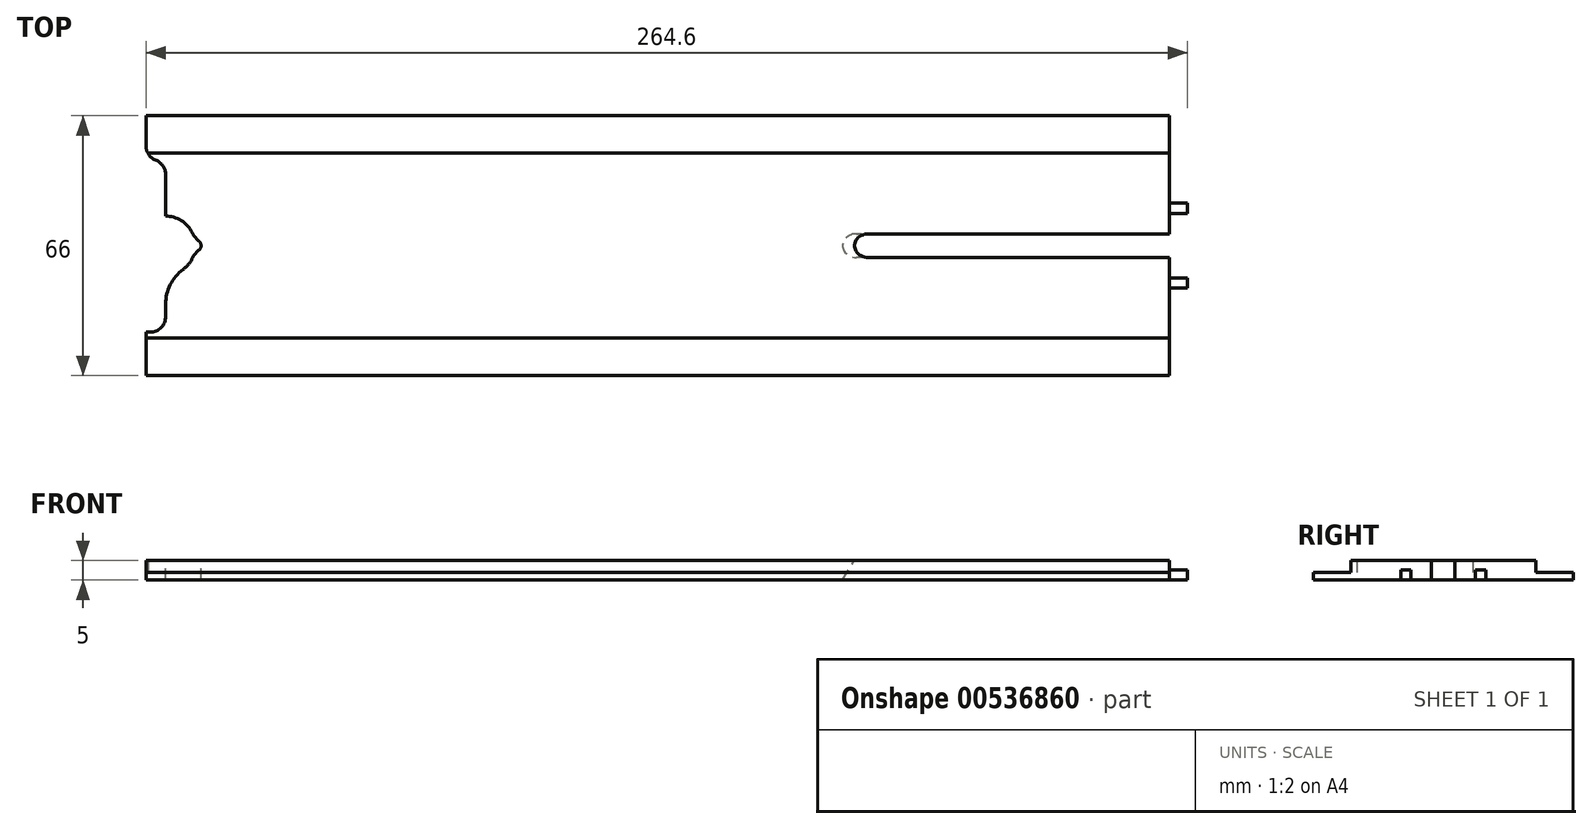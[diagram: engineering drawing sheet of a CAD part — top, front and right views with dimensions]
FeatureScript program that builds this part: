
annotation { "Feature Type Name" : "Feature", "Feature Type Description" : "" }
export const myFeature = defineFeature(function(context is Context, id is Id, definition is map)
    precondition{}
    {
        {
            var Q0;
            Q0=qCreatedBy(makeId("Top.planeOp"),FACE);
            var sketch = newSketch(context, id + "F0", { "sketchPlane" : qUnion([Q0])});
            skLineSegment(sketch, "E0.bottom", {"start": v(-61.94, 24.83) * mm, "end": v(198.06, 24.83) * mm});
            skLineSegment(sketch, "E0.top", {"start": v(-61.94, -41.17) * mm, "end": v(198.06, -41.17) * mm});
            skLineSegment(sketch, "E0.left", {"start": v(-61.94, 24.83) * mm, "end": v(-61.94, -41.17) * mm});
            skLineSegment(sketch, "E0.right", {"start": v(198.06, 24.83) * mm, "end": v(198.06, -41.17) * mm});
            skSolve(sketch);
        }
        {
            var Q0;
            Q0=makeQuery(id+"F0.imprint","IMPRINT",FACE,{"disambiguationData":[TD([[makeQuery(id+"F0.imprint","IMPRINT",EDGE,{"derivedFrom":sQuery(id+"F0.wireOp",EDGE,"E0.bottom")}),-1.0]])]});
            extrude(context, id + "F1", {"entities" : qUnion([Q0]), "depth" : 2 * mm, "offsetDistance" : 25 * mm});
        }
        {
            var Q0;
            Q0=makeQuery(id+"F1.opExtrude","CAP_FACE",FACE,{"disambiguationData":[OSD([sQuery(id+"F0.wireOp",EDGE,"E0.bottom"),sQuery(id+"F0.wireOp",EDGE,"E0.top"),sQuery(id+"F0.wireOp",EDGE,"E0.left"),sQuery(id+"F0.wireOp",EDGE,"E0.right")])],"isStart":false});
            var sketch = newSketch(context, id + "F2", { "sketchPlane" : qUnion([Q0])});
            skLineSegment(sketch, "E1.bottom", {"start": v(-61.94, 15.33) * mm, "end": v(198.06, 15.33) * mm});
            skLineSegment(sketch, "E1.top", {"start": v(-61.94, -31.67) * mm, "end": v(198.06, -31.67) * mm});
            skLineSegment(sketch, "E1.left", {"start": v(-61.94, 15.33) * mm, "end": v(-61.94, -31.67) * mm});
            skLineSegment(sketch, "E1.right", {"start": v(198.06, 15.33) * mm, "end": v(198.06, -31.67) * mm});
            skSolve(sketch);
        }
        {
            var Q0;
            Q0=qSketchRegion(id+"F2",true);
            extrude(context, id + "F3", {"entities" : qUnion([Q0]), "operationType" : NewBodyOperationType.ADD, "depth" : 3 * mm, "offsetDistance" : 25 * mm});
        }
        {
            var Q0;
            Q0=makeQuery(id+"F3.opExtrude","CAP_FACE",FACE,{"disambiguationData":[OSD([sQuery(id+"F2.wireOp",EDGE,"E1.bottom"),sQuery(id+"F2.wireOp",EDGE,"E1.top"),sQuery(id+"F2.wireOp",EDGE,"E1.left"),sQuery(id+"F2.wireOp",EDGE,"E1.right")])],"isStart":false});
            var sketch = newSketch(context, id + "F4", { "sketchPlane" : qUnion([Q0])});
            skLineSegment(sketch, "E2", {"start": v(198.06, -8.17) * mm, "end": v(-61.94, -8.17) * mm, "construction": true});
            skLineSegment(sketch, "E3.bottom", {"start": v(198.06, -5.17) * mm, "end": v(118.06, -5.17) * mm});
            skLineSegment(sketch, "E3.top", {"start": v(198.06, -11.17) * mm, "end": v(118.06, -11.17) * mm});
            skLineSegment(sketch, "E3.left", {"start": v(198.06, -5.17) * mm, "end": v(198.06, -11.17) * mm});
            skLineSegment(sketch, "E3.right", {"start": v(118.06, -5.17) * mm, "end": v(118.06, -11.17) * mm});
            skPoint(sketch, "E4", {"position": v(118.06, -8.17) * mm});
            skSolve(sketch);
        }
        {
            var Q0;
            Q0=qSketchRegion(id+"F4",true);
            extrude(context, id + "F5", {"entities" : qUnion([Q0]), "operationType" : NewBodyOperationType.REMOVE, "oppositeDirection" : true, "depth" : 25 * mm, "offsetDistance" : 25 * mm});
        }
        {
            var Q0;
            Q0=makeQuery(id+"F5.boolean.opBoolean","INTERSECT",EDGE,{"derivedFrom":[makeQuery(id+"F1.opExtrude","CAP_FACE",FACE,{"disambiguationData":[OSD([sQuery(id+"F0.wireOp",EDGE,"E0.bottom"),sQuery(id+"F0.wireOp",EDGE,"E0.top"),sQuery(id+"F0.wireOp",EDGE,"E0.left"),sQuery(id+"F0.wireOp",EDGE,"E0.right")])],"isStart":true}),makeQuery(id+"F5.opExtrude","SWEPT_FACE",FACE,{"disambiguationData":[OSD([sQuery(id+"F4.wireOp",EDGE,"E3.right")])]})]});
            chamfer(context, id + "F6", {"entities" : qUnion([Q0]), "chamferType" : ChamferType.TWO_OFFSETS, "width1" : 3 * mm, "oppositeDirection" : false, "width2" : 5 * mm, "tangentPropagation" : true});
        }
        {
            var Q0;
            Q0=makeQuery(id+"F6.opChamfer","BLEND_EDGE",EDGE,{"blendedFrom":[makeQuery(id+"F5.boolean.opBoolean","INTERSECT",EDGE,{"derivedFrom":[makeQuery(id+"F1.opExtrude","CAP_FACE",FACE,{"disambiguationData":[OSD([sQuery(id+"F0.wireOp",EDGE,"E0.bottom"),sQuery(id+"F0.wireOp",EDGE,"E0.top"),sQuery(id+"F0.wireOp",EDGE,"E0.left"),sQuery(id+"F0.wireOp",EDGE,"E0.right")])],"isStart":true}),makeQuery(id+"F5.opExtrude","SWEPT_FACE",FACE,{"disambiguationData":[OSD([sQuery(id+"F4.wireOp",EDGE,"E3.right")])]})]}),makeQuery(id+"F5.boolean.opBoolean","COPY",FACE,{"derivedFrom":makeQuery(id+"F5.opExtrude","SWEPT_FACE",FACE,{"disambiguationData":[OSD([sQuery(id+"F4.wireOp",EDGE,"E3.top")])]})})],"blendedInto":[makeQuery(id+"F5.boolean.opBoolean","COPY",FACE,{"derivedFrom":makeQuery(id+"F5.opExtrude","SWEPT_FACE",FACE,{"disambiguationData":[OSD([sQuery(id+"F4.wireOp",EDGE,"E3.top")])]})})]});
            var Q1;
            Q1=makeQuery(id+"F6.opChamfer","BLEND_EDGE",EDGE,{"blendedFrom":[makeQuery(id+"F5.boolean.opBoolean","INTERSECT",EDGE,{"derivedFrom":[makeQuery(id+"F1.opExtrude","CAP_FACE",FACE,{"disambiguationData":[OSD([sQuery(id+"F0.wireOp",EDGE,"E0.bottom"),sQuery(id+"F0.wireOp",EDGE,"E0.top"),sQuery(id+"F0.wireOp",EDGE,"E0.left"),sQuery(id+"F0.wireOp",EDGE,"E0.right")])],"isStart":true}),makeQuery(id+"F5.opExtrude","SWEPT_FACE",FACE,{"disambiguationData":[OSD([sQuery(id+"F4.wireOp",EDGE,"E3.right")])]})]}),makeQuery(id+"F5.boolean.opBoolean","COPY",FACE,{"derivedFrom":makeQuery(id+"F5.opExtrude","SWEPT_FACE",FACE,{"disambiguationData":[OSD([sQuery(id+"F4.wireOp",EDGE,"E3.bottom")])]})})],"blendedInto":[makeQuery(id+"F5.boolean.opBoolean","COPY",FACE,{"derivedFrom":makeQuery(id+"F5.opExtrude","SWEPT_FACE",FACE,{"disambiguationData":[OSD([sQuery(id+"F4.wireOp",EDGE,"E3.bottom")])]})})]});
            fillet(context, id + "F7", {"entities" : qUnion([Q0, Q1]), "radius" : 3 * mm, "tangentPropagation" : true, "allowEdgeOverflow" : false});
        }
        {
            var Q0;
            Q0=makeQuery(id+"F1.opExtrude","CAP_FACE",FACE,{"disambiguationData":[OSD([sQuery(id+"F0.wireOp",EDGE,"E0.bottom"),sQuery(id+"F0.wireOp",EDGE,"E0.top"),sQuery(id+"F0.wireOp",EDGE,"E0.left"),sQuery(id+"F0.wireOp",EDGE,"E0.right")])],"isStart":true});
            var sketch = newSketch(context, id + "F8", { "sketchPlane" : qUnion([Q0])});
            skLineSegment(sketch, "E5.bottom", {"start": v(-61.94, 30.17) * mm, "end": v(-56.94, 30.17) * mm});
            skLineSegment(sketch, "E5.top", {"start": v(-61.94, -13.83) * mm, "end": v(-56.94, -13.83) * mm});
            skLineSegment(sketch, "E5.left", {"start": v(-61.94, 30.17) * mm, "end": v(-61.94, -13.83) * mm});
            skLineSegment(sketch, "E5.right", {"start": v(-56.94, 30.17) * mm, "end": v(-56.94, -13.83) * mm});
            skPoint(sketch, "E6", {"position": v(-61.94, 8.17) * mm});
            skSolve(sketch);
        }
        {
            var Q0;
            Q0=makeQuery(id+"F8.imprint","IMPRINT",FACE,{"disambiguationData":[TD([[makeQuery(id+"F8.imprint","IMPRINT",EDGE,{"derivedFrom":sQuery(id+"F8.wireOp",EDGE,"E5.bottom")}),-1.0]])]});
            extrude(context, id + "F9", {"entities" : qUnion([Q0]), "operationType" : NewBodyOperationType.REMOVE, "oppositeDirection" : true, "depth" : 25 * mm, "offsetDistance" : 25 * mm});
        }
        {
            var Q0;
            Q0=makeQuery(id+"F9.boolean.opBoolean","COPY",EDGE,{"derivedFrom":makeQuery(id+"F9.opExtrude","SWEPT_EDGE",EDGE,{"disambiguationData":[OSD([sQuery(id+"F8.wireOp",EDGE,"E5.bottom"),sQuery(id+"F8.wireOp",EDGE,"E5.right")])]})});
            var Q1;
            Q1=makeQuery(id+"F9.boolean.opBoolean","COPY",EDGE,{"derivedFrom":makeQuery(id+"F9.opExtrude","SWEPT_EDGE",EDGE,{"disambiguationData":[OSD([sQuery(id+"F8.wireOp",EDGE,"E5.top"),sQuery(id+"F8.wireOp",EDGE,"E5.right")])]})});
            fillet(context, id + "F10", {"entities" : qUnion([Q0, Q1]), "radius" : 4 * mm, "tangentPropagation" : true, "allowEdgeOverflow" : false});
        }
        {
            var Q0;
            Q0=makeQuery(id+"F1.opExtrude","CAP_FACE",FACE,{"disambiguationData":[OSD([sQuery(id+"F0.wireOp",EDGE,"E0.bottom"),sQuery(id+"F0.wireOp",EDGE,"E0.top"),sQuery(id+"F0.wireOp",EDGE,"E0.left"),sQuery(id+"F0.wireOp",EDGE,"E0.right")])],"isStart":true});
            var sketch = newSketch(context, id + "F11", { "sketchPlane" : qUnion([Q0])});
            skCircle(sketch, "E7", {"center": v(-56.94, 8.17) * mm, "radius": 7.5 * mm});
            skSolve(sketch);
        }
        {
            var Q0;
            {var subQ0=sQuery(id+"F11.wireOp",EDGE,"E7");var subQ1=makeQuery(id+"F9.boolean.opBoolean","COPY",EDGE,{"derivedFrom":makeQuery(id+"F9.opExtrude","CAP_EDGE",EDGE,{"disambiguationData":[OSD([sQuery(id+"F8.wireOp",EDGE,"E5.right")])],"isStart":true})});var subQ2=makeQuery(id+"F11.imprint","INTERSECT",VERTEX,{"disambiguationData":[OD(0.0)],"derivedFrom":[subQ1,subQ0]});Q0=makeQuery(id+"F11.imprint","IMPRINT",FACE,{"disambiguationData":[TD([[makeQuery(id+"F11.imprint","IMPRINT",EDGE,{"disambiguationData":[TD([[subQ2,1.0]])],"derivedFrom":subQ0}),1.0]])]});}
            extrude(context, id + "F12", {"entities" : qUnion([Q0]), "operationType" : NewBodyOperationType.REMOVE, "oppositeDirection" : true, "depth" : 25 * mm, "offsetDistance" : 25 * mm});
        }
        {
            var Q0;
            {var subQ0=sQuery(id+"F11.wireOp",EDGE,"E7");var subQ1=sQuery(id+"F8.wireOp",EDGE,"E5.right");Q0=makeQuery(id+"F12.boolean.opBoolean","COPY",EDGE,{"derivedFrom":makeQuery(id+"F12.opExtrude","SWEPT_EDGE",EDGE,{"disambiguationData":[OSD([subQ1,subQ0]),TDD([makeQuery(id+"F11.imprint","INTERSECT",VERTEX,{"disambiguationData":[OD(0.0)],"derivedFrom":[makeQuery(id+"F9.boolean.opBoolean","COPY",EDGE,{"derivedFrom":makeQuery(id+"F9.opExtrude","CAP_EDGE",EDGE,{"disambiguationData":[OSD([subQ1])],"isStart":true})}),subQ0]})])]})});}
            var Q1;
            {var subQ0=sQuery(id+"F11.wireOp",EDGE,"E7");var subQ1=sQuery(id+"F8.wireOp",EDGE,"E5.right");Q1=makeQuery(id+"F12.boolean.opBoolean","COPY",EDGE,{"derivedFrom":makeQuery(id+"F12.opExtrude","SWEPT_EDGE",EDGE,{"disambiguationData":[OSD([subQ1,subQ0]),TDD([makeQuery(id+"F11.imprint","INTERSECT",VERTEX,{"disambiguationData":[OD(1.0)],"derivedFrom":[makeQuery(id+"F9.boolean.opBoolean","COPY",EDGE,{"derivedFrom":makeQuery(id+"F9.opExtrude","CAP_EDGE",EDGE,{"disambiguationData":[OSD([subQ1])],"isStart":true})}),subQ0]})])]})});}
            fillet(context, id + "F13", {"entities" : qUnion([Q0, Q1]), "radius" : 11 * mm, "tangentPropagation" : true, "allowEdgeOverflow" : false});
        }
        {
            var Q0;
            Q0=makeQuery(id+"F1.opExtrude","CAP_FACE",FACE,{"disambiguationData":[OSD([sQuery(id+"F0.wireOp",EDGE,"E0.bottom"),sQuery(id+"F0.wireOp",EDGE,"E0.top"),sQuery(id+"F0.wireOp",EDGE,"E0.left"),sQuery(id+"F0.wireOp",EDGE,"E0.right")])],"isStart":true});
            var sketch = newSketch(context, id + "F14", { "sketchPlane" : qUnion([Q0])});
            skLineSegment(sketch, "E8.bottom", {"start": v(-41.33, 41.17) * mm, "end": v(198.06, 41.17) * mm});
            skLineSegment(sketch, "E8.top", {"start": v(-41.33, -24.83) * mm, "end": v(198.06, -24.83) * mm});
            skLineSegment(sketch, "E8.left", {"start": v(-41.33, 41.17) * mm, "end": v(-41.33, -24.83) * mm});
            skLineSegment(sketch, "E8.right", {"start": v(198.06, 41.17) * mm, "end": v(198.06, -24.83) * mm});
            skSolve(sketch);
        }
        {
            var Q0;
            Q0=makeQuery(id+"F1.opExtrude","CAP_FACE",FACE,{"disambiguationData":[OSD([sQuery(id+"F0.wireOp",EDGE,"E0.bottom"),sQuery(id+"F0.wireOp",EDGE,"E0.top"),sQuery(id+"F0.wireOp",EDGE,"E0.left"),sQuery(id+"F0.wireOp",EDGE,"E0.right")])],"isStart":true});
            var sketch = newSketch(context, id + "F15", { "sketchPlane" : qUnion([Q0])});
            skLineSegment(sketch, "E9.bottom", {"start": v(198.06, 19.17) * mm, "end": v(193.06, 19.17) * mm});
            skLineSegment(sketch, "E9.top", {"start": v(198.06, 16.17) * mm, "end": v(193.06, 16.17) * mm});
            skLineSegment(sketch, "E9.left", {"start": v(198.06, 19.17) * mm, "end": v(198.06, 16.17) * mm});
            skLineSegment(sketch, "E9.right", {"start": v(193.06, 19.17) * mm, "end": v(193.06, 16.17) * mm});
            skPoint(sketch, "E10", {"position": v(198.06, 17.67) * mm});
            skSolve(sketch);
        }
        {
            var Q0;
            Q0=makeQuery(id+"F1.opExtrude","CAP_FACE",FACE,{"disambiguationData":[OSD([sQuery(id+"F0.wireOp",EDGE,"E0.bottom"),sQuery(id+"F0.wireOp",EDGE,"E0.top"),sQuery(id+"F0.wireOp",EDGE,"E0.left"),sQuery(id+"F0.wireOp",EDGE,"E0.right")])],"isStart":true});
            var sketch = newSketch(context, id + "F16", { "sketchPlane" : qUnion([Q0])});
            skLineSegment(sketch, "E11.bottom", {"start": v(198.06, 0.17) * mm, "end": v(193.06, 0.17) * mm});
            skLineSegment(sketch, "E11.top", {"start": v(198.06, -2.83) * mm, "end": v(193.06, -2.83) * mm});
            skLineSegment(sketch, "E11.left", {"start": v(198.06, 0.17) * mm, "end": v(198.06, -2.83) * mm});
            skLineSegment(sketch, "E11.right", {"start": v(193.06, 0.17) * mm, "end": v(193.06, -2.83) * mm});
            skSolve(sketch);
        }
        {
            var Q0;
            Q0=makeQuery(id+"F9.boolean.opBoolean","COPY",EDGE,{"derivedFrom":makeQuery(id+"F9.opExtrude","SWEPT_EDGE",EDGE,{"disambiguationData":[OSD([sQuery(id+"F0.wireOp",EDGE,"E0.left"),sQuery(id+"F8.wireOp",EDGE,"E5.top"),sQuery(id+"F8.wireOp",EDGE,"E5.left")])]})});
            var Q1;
            Q1=makeQuery(id+"F9.boolean.opBoolean","COPY",EDGE,{"derivedFrom":makeQuery(id+"F9.opExtrude","SWEPT_EDGE",EDGE,{"disambiguationData":[OSD([sQuery(id+"F0.wireOp",EDGE,"E0.left"),sQuery(id+"F8.wireOp",EDGE,"E5.bottom"),sQuery(id+"F8.wireOp",EDGE,"E5.left")])]})});
            fillet(context, id + "F17", {"entities" : qUnion([Q0, Q1]), "radius" : 4 * mm, "tangentPropagation" : true, "allowEdgeOverflow" : false});
        }
        {
            var Q0;
            Q0=makeQuery(id+"F3.opExtrude","CAP_FACE",FACE,{"disambiguationData":[OSD([sQuery(id+"F2.wireOp",EDGE,"E1.bottom"),sQuery(id+"F2.wireOp",EDGE,"E1.top"),sQuery(id+"F2.wireOp",EDGE,"E1.left"),sQuery(id+"F2.wireOp",EDGE,"E1.right")])],"isStart":false});
            var sketch = newSketch(context, id + "F18", { "sketchPlane" : qUnion([Q0])});
            skCircle(sketch, "E12", {"center": v(-49.44, -8.17) * mm, "radius": 1.5 * mm});
            skSolve(sketch);
        }
        {
            var Q0;
            Q0=qSketchRegion(id+"F18",true);
            extrude(context, id + "F19", {"entities" : qUnion([Q0]), "operationType" : NewBodyOperationType.REMOVE, "oppositeDirection" : true, "depth" : 25 * mm, "offsetDistance" : 25 * mm});
        }
        {
            var Q0;
            Q0=makeQuery(id+"F19.boolean.opBoolean","INTERSECT",EDGE,{"disambiguationData":[OD(0.0)],"derivedFrom":[makeQuery(id+"F12.boolean.opBoolean","COPY",FACE,{"derivedFrom":makeQuery(id+"F12.opExtrude","SWEPT_FACE",FACE,{"disambiguationData":[OSD([sQuery(id+"F11.wireOp",EDGE,"E7")])]})}),makeQuery(id+"F19.opExtrude","SWEPT_FACE",FACE,{"disambiguationData":[OSD([sQuery(id+"F18.wireOp",EDGE,"E12")])]})]});
            var Q1;
            Q1=makeQuery(id+"F19.boolean.opBoolean","INTERSECT",EDGE,{"disambiguationData":[OD(1.0)],"derivedFrom":[makeQuery(id+"F12.boolean.opBoolean","COPY",FACE,{"derivedFrom":makeQuery(id+"F12.opExtrude","SWEPT_FACE",FACE,{"disambiguationData":[OSD([sQuery(id+"F11.wireOp",EDGE,"E7")])]})}),makeQuery(id+"F19.opExtrude","SWEPT_FACE",FACE,{"disambiguationData":[OSD([sQuery(id+"F18.wireOp",EDGE,"E12")])]})]});
            fillet(context, id + "F20", {"entities" : qUnion([Q0, Q1]), "radius" : 6 * mm, "tangentPropagation" : true, "allowEdgeOverflow" : false});
        }
        {
            var Q0;
            {var subQ0=sQuery(id+"F2.wireOp",EDGE,"E1.right");var subQ2=sQuery(id+"F0.wireOp",EDGE,"E0.top");var subQ3=sQuery(id+"F0.wireOp",EDGE,"E0.right");Q0=makeQuery(id+"F5.boolean.opBoolean","SPLIT",FACE,{"disambiguationData":[TD([makeQuery(id+"F1.opExtrude","SWEPT_FACE",FACE,{"disambiguationData":[OSD([subQ2])]})])],"derivedFrom":makeQuery(id+"F3.boolean.opBoolean","MERGE",FACE,{"derivedFrom":[makeQuery(id+"F1.opExtrude","SWEPT_FACE",FACE,{"disambiguationData":[OSD([subQ3])]}),makeQuery(id+"F3.opExtrude","SWEPT_FACE",FACE,{"disambiguationData":[OSD([subQ0])]})]})});}
            var sketch = newSketch(context, id + "F21", { "sketchPlane" : qUnion([Q0])});
            skLineSegment(sketch, "E13.bottom", {"start": v(-16.37, 0) * mm, "end": v(-18.97, 0) * mm});
            skLineSegment(sketch, "E13.top", {"start": v(-16.37, 2.6) * mm, "end": v(-18.97, 2.6) * mm});
            skLineSegment(sketch, "E13.left", {"start": v(-16.37, 0) * mm, "end": v(-16.37, 2.6) * mm});
            skLineSegment(sketch, "E13.right", {"start": v(-18.97, 0) * mm, "end": v(-18.97, 2.6) * mm});
            skLineSegment(sketch, "E14.bottom", {"start": v(0.03, 0) * mm, "end": v(2.63, 0) * mm});
            skLineSegment(sketch, "E14.top", {"start": v(0.03, 2.6) * mm, "end": v(2.63, 2.6) * mm});
            skLineSegment(sketch, "E14.left", {"start": v(0.03, 0) * mm, "end": v(0.03, 2.6) * mm});
            skLineSegment(sketch, "E14.right", {"start": v(2.63, 0) * mm, "end": v(2.63, 2.6) * mm});
            skSolve(sketch);
        }
        {
            var Q0;
            Q0 = qSketchRegion(id + "F21", true);
            extrude(context, id + "F22", {"entities" : qUnion([Q0]), "depth" : 4.6 * mm, "offsetDistance" : 25 * mm});
        }
    });
